# Revit family: Haworth_Upside_HeightAdjustTable_Rectangle_SingleStage_Credenza
name_source: partatom
category: Furniture Systems
units: mm (PartAtom-declared; Revit-internal decimal feet)

## family parameters
Always vertical = Yes
Cut with Voids When Loaded = No
OmniClass Number = 23.40.70.14.64.21
OmniClass Title = Systems Furniture
Part Type = Normal
Room Calculation Point = No
Round Connector Dimension = Use Diameter
Shared = No
Work Plane-Based = No

## types (7) — shared parameters
Actual Height = 29"
Assembly Code = E2020200
Custom Size = No
Description = Haworth - Upside HAT Rectangular - Standard Range
Height = 29"
Leg Height = 27 13/16"
Leg Offset = 3 1/32"
Manufacturer = Haworth
Max. Depth = 29"
Max. Height = 46 77/128"
Max. Width = 82"
Min. Depth = 23"
Min. Height = 27 51/128"
Min. Width = 46"
Min/Max Width = 46-82 in. @ 6 in. increments
Model = TJRA
Paddle Finish = Haworth _ Paint _ Black
Paddle Offset = 0"
Revision Number = 1
Size = Verify Final Dim. w/ Haworth
Standard Depths = 23, 29 in.
Table Thickness = 1 3/16"
URL = http://www.haworth.com
URL - Product = http://www.haworth.com
Warranty = http://www.haworth.com

## per-type parameters (varying)
| type | 23in. Depth | 29in. Depth | Actual Depth | Actual Width | C-Leg | Front Leg Offset | Rail Location | T-Leg | Width |
| 82w 29d - T-Leg | No | Yes | 29" | 82" | No | 1/2" | 14 3/8" | Yes | 82" |
| 76w 29d - C-Leg | No | Yes | 29" | 76" | Yes | 0" | 20 1/32" | No | 76" |
| 70w 29d - T-Leg | No | Yes | 29" | 70" | No | 1/2" | 14 3/8" | Yes | 70" |
| 64w 29d - C-Leg | No | Yes | 29" | 64" | Yes | 0" | 20 1/32" | No | 64" |
| 58w 23d - T-Leg | Yes | No | 23" | 58" | No | 1/2" | 11 5/16" | Yes | 58" |
| 46w 23d - T-Leg | Yes | No | 23" | 46" | No | 1/2" | 11 5/16" | Yes | 46" |
| 52w 23d - T-Leg | Yes | No | 23" | 52" | No | 1/2" | 11 5/16" | Yes | 52" |

## geometry (parser evidence)
native form markers: Sweep x9
no freeform markers — native parametric forms only
